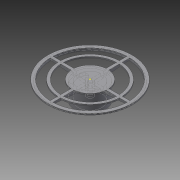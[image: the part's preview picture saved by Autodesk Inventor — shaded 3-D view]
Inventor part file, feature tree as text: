
AUTODESK INVENTOR PART (.ipt)
format: ipt  version: 2015 (Build 190159000, 159)  size: 336,896 bytes
history: native  units: mm
features: sketch x12, extrude x10, chamfer x9, hole x1
ambient origin geometry x8: Origin, YZ Plane, XZ Plane, XY Plane, X Axis, Y Axis, Z Axis, Center Point
bodies: Solid1 (feature_tree)
feature tree (32):
  extrude  "Extrusion1"  Depth=10.0mm
  extrude  "Extrusion2"  Depth=20.0mm
  extrude  "Extrusion3"  Depth=2.0mm
  chamfer  "Chamfer1"  Distance=1.5mm
  chamfer  "Chamfer2"  Distance=1.5mm Angle=45.0deg
  chamfer  "Chamfer3"  Distance=1.5mm Angle=45.0deg
  chamfer  "Chamfer4"  Distance=1.5mm Angle=45.0deg
  hole  "Hole1"  [1 undecoded]
  sketch  "Sketch5"  dims[d9=2.0mm]
  extrude  "Extrusion4"  Depth=55.0mm
  chamfer  "Chamfer5"  Distance=55.0mm
  extrude  "Extrusion5"  Depth=55.0mm
  extrude  "Extrusion6"  Depth=55.0mm
  chamfer  "Chamfer6"  Distance=2.0mm
  chamfer  "Chamfer7"  Distance=1.5mm Angle=45.0deg
  chamfer  "Chamfer8"  Distance=5.0mm
  chamfer  "Chamfer9"  Distance=120.0mm
  extrude  "Extrusion7"  Depth=2.0mm TaperAngle=0.0deg
  extrude  "Extrusion8"  Depth=5.0mm TaperAngle=0.0deg
  extrude  "Extrusion9"  Depth=55.0mm
  extrude  "Extrusion10"  Depth=55.0mm
  sketch  "Sketch1"  dims[d0=5.2mm d1=10.0mm]
  sketch  "Sketch2"  dims[d2=20.0mm d3=0.0mm d4=50.0mm]
  sketch  "Sketch3"  dims[d5=2.0mm d6=0.0mm d7=2.0mm]
  sketch  "Sketch4"  dims[d8=2.0mm]
  sketch  "Sketch6"  dims[d10=2.0mm]
  sketch  "Sketch7"  dims[d11=22.0mm]
  sketch  "Sketch8"  dims[d12=22.0mm]
  sketch  "Sketch9"  dims[d13=22.0mm]
  sketch  "Sketch10"  dims[d14=22.0mm]
  sketch  "Sketch11"  dims[d15=2.7mm d16=1.5mm d17=0.0mm d18=1.5mm d19=2.0mm d20=45.0deg d21=1.5mm d22=2.0mm d23=45.0deg d24=1.5mm d25=2.0mm d26=45.0deg]
  sketch  "Sketch12"  dims[d27=1.5mm d28=2.0mm d29=45.0deg d30=10.0mm d31=3.0mm d32=6.0mm d33=4.0mm d34=2.0mm d35=90.0deg d36=8.0mm d37=20.594885mm d38=55.0mm d39=55.0mm d40=55.0mm d41=55.0mm d42=2.0mm d43=0.0mm d44=1.5mm d45=2.0mm d46=45.0deg d47=5.0mm d48=120.0mm d49=2.0mm d50=0.0mm d51=5.0mm d52=0.0mm d53=55.0mm d54=5.0mm d55=4.363323mm d56=55.0mm d57=5.0mm d58=4.363323mm d59=55.0mm d60=5.0mm d61=4.363323mm d62=55.0mm d63=5.0mm d64=4.363323mm d65=80.0mm d66=88.0mm d67=2.0mm d68=0.0mm d69=110.0mm d70=2.0mm d71=2.0mm d72=0.0mm d73=34.0mm d74=5.0mm d75=24.5mm d76=0.0mm d77=19.5mm d78=0.0mm]
note: 1 required parameter value undecoded (feature->parameter linkage not recoverable at this tier; creation-order binding heuristic only, values carry confidence <= 0.55)
